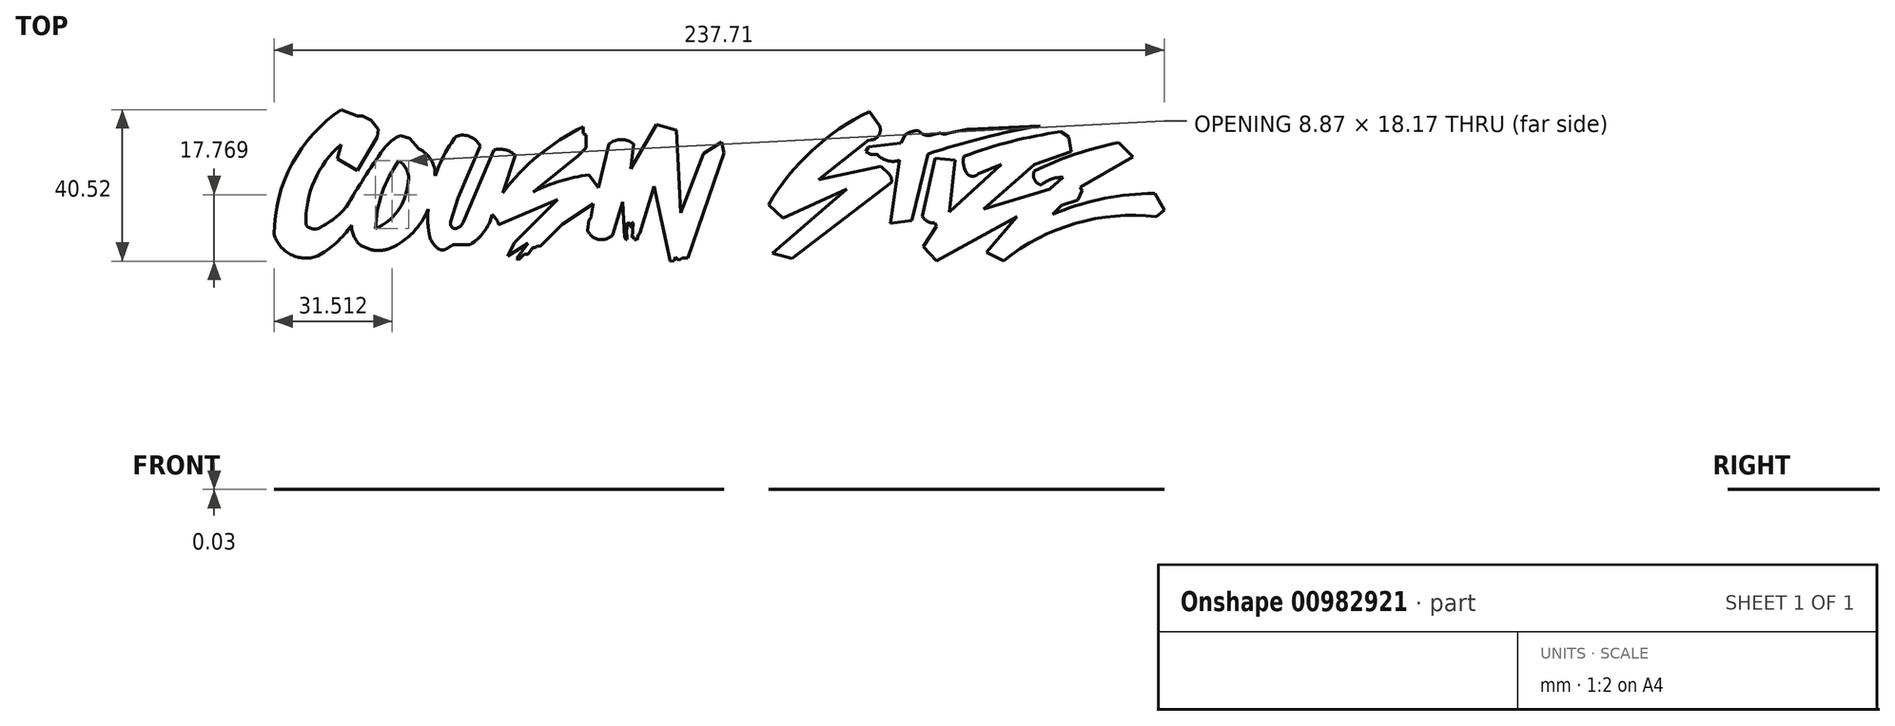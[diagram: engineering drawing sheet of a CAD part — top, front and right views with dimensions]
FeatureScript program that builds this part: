
annotation { "Feature Type Name" : "Feature", "Feature Type Description" : "" }
export const myFeature = defineFeature(function(context is Context, id is Id, definition is map)
    precondition{}
    {
        {
            var Q0;
            Q0=qCreatedBy(makeId("Top.planeOp"),FACE);
            var sketch = newSketch(context, id + "F0", { "sketchPlane" : qUnion([Q0])});
            skLineSegment(sketch, "E0", {"start": v(-35.46, -23.34) * mm, "end": v(-30.17, -14.33) * mm});
            skLineSegment(sketch, "E1", {"start": v(-30.17, -14.33) * mm, "end": v(-29.84, -12.23) * mm});
            skLineSegment(sketch, "E2", {"start": v(-29.84, -12.23) * mm, "end": v(-31.77, -9.82) * mm});
            skLineSegment(sketch, "E3", {"start": v(-31.77, -9.82) * mm, "end": v(-34.06, -8.67) * mm});
            skLineSegment(sketch, "E4", {"start": v(-34.06, -8.67) * mm, "end": v(-35.46, -8.67) * mm});
            skLineSegment(sketch, "E5", {"start": v(-35.46, -8.67) * mm, "end": v(-39.77, -7) * mm});
            skArc(sketch, "E6", {"start": v(-39.77, -7) * mm, "mid": v(-52.88, -21.43) * mm, "end": v(-57.73, -40.32) * mm});
            skArc(sketch, "E7", {"start": v(-57.73, -40.32) * mm, "mid": v(-53.23, -45.73) * mm, "end": v(-46.2, -46.17) * mm});
            skArc(sketch, "E8", {"start": v(-46.2, -46.17) * mm, "mid": v(-41.12, -42.57) * mm, "end": v(-37.05, -37.85) * mm});
            skArc(sketch, "E9", {"start": v(-37.05, -37.85) * mm, "mid": v(-36.37, -40.9) * mm, "end": v(-34.48, -43.39) * mm});
            skLineSegment(sketch, "E10", {"start": v(-34.48, -43.39) * mm, "end": v(-31.63, -44.47) * mm});
            skArc(sketch, "E11", {"start": v(-31.63, -44.47) * mm, "mid": v(-29.09, -44.6) * mm, "end": v(-26.6, -44.04) * mm});
            skArc(sketch, "E12", {"start": v(-26.6, -44.04) * mm, "mid": v(-20.56, -39.76) * mm, "end": v(-16.55, -33.54) * mm});
            skArc(sketch, "E13", {"start": v(-16.55, -33.54) * mm, "mid": v(-16.67, -36) * mm, "end": v(-16.55, -38.47) * mm});
            skArc(sketch, "E14", {"start": v(-16.55, -38.47) * mm, "mid": v(-16.38, -39.69) * mm, "end": v(-16.17, -40.9) * mm});
            skArc(sketch, "E15", {"start": v(-16.17, -40.9) * mm, "mid": v(-15.26, -42.78) * mm, "end": v(-13.74, -44.22) * mm});
            skArc(sketch, "E16", {"start": v(-13.74, -44.22) * mm, "mid": v(-12.76, -44.51) * mm, "end": v(-11.77, -44.22) * mm});
            skArc(sketch, "E17", {"start": v(-11.77, -44.22) * mm, "mid": v(-10.82, -43.68) * mm, "end": v(-9.93, -43.06) * mm});
            skLineSegment(sketch, "E18", {"start": v(-9.93, -43.06) * mm, "end": v(-5.36, -43.06) * mm});
            skArc(sketch, "E19", {"start": v(-5.36, -43.06) * mm, "mid": v(-1.64, -39.67) * mm, "end": v(0.5, -35.13) * mm});
            skArc(sketch, "E20", {"start": v(2.27, -37.75) * mm, "mid": v(1.61, -36.3) * mm, "end": v(0.5, -35.13) * mm});
            skLineSegment(sketch, "E21", {"start": v(2.27, -37.75) * mm, "end": v(17.92, -31.07) * mm});
            skLineSegment(sketch, "E22", {"start": v(17.92, -31.07) * mm, "end": v(6.59, -42.5) * mm});
            skLineSegment(sketch, "E23", {"start": v(6.59, -42.5) * mm, "end": v(4.59, -46.12) * mm});
            skLineSegment(sketch, "E24", {"start": v(4.59, -46.12) * mm, "end": v(10.13, -42.66) * mm});
            skLineSegment(sketch, "E25", {"start": v(10.13, -42.66) * mm, "end": v(7, -46.8) * mm});
            skLineSegment(sketch, "E26", {"start": v(7, -46.8) * mm, "end": v(7.56, -47.1) * mm});
            skLineSegment(sketch, "E27", {"start": v(7.56, -47.1) * mm, "end": v(9.08, -45.58) * mm});
            skLineSegment(sketch, "E28", {"start": v(9.08, -45.58) * mm, "end": v(10.12, -45.58) * mm});
            skLineSegment(sketch, "E29", {"start": v(10.12, -45.58) * mm, "end": v(11.39, -43.92) * mm});
            skLineSegment(sketch, "E30", {"start": v(11.39, -43.92) * mm, "end": v(12.1, -43.92) * mm});
            skLineSegment(sketch, "E31", {"start": v(12.1, -43.92) * mm, "end": v(12.7, -43.32) * mm});
            skLineSegment(sketch, "E32", {"start": v(12.7, -43.32) * mm, "end": v(13.26, -43.63) * mm});
            skLineSegment(sketch, "E33", {"start": v(13.26, -43.63) * mm, "end": v(19.23, -37.6) * mm});
            skLineSegment(sketch, "E34", {"start": v(19.23, -37.6) * mm, "end": v(27.54, -32.23) * mm});
            skLineSegment(sketch, "E35", {"start": v(27.54, -32.23) * mm, "end": v(26.9, -36) * mm});
            skLineSegment(sketch, "E36", {"start": v(26.9, -36) * mm, "end": v(26.4, -36.5) * mm});
            skLineSegment(sketch, "E37", {"start": v(26.4, -36.5) * mm, "end": v(26.02, -39.3) * mm});
            skArc(sketch, "E38", {"start": v(26.02, -39.3) * mm, "mid": v(29.05, -41.7) * mm, "end": v(32.72, -40.48) * mm});
            skLineSegment(sketch, "E39", {"start": v(32.72, -40.48) * mm, "end": v(35.35, -31.71) * mm});
            skLineSegment(sketch, "E40", {"start": v(35.35, -31.71) * mm, "end": v(35.84, -41.17) * mm});
            skLineSegment(sketch, "E41", {"start": v(35.84, -41.17) * mm, "end": v(36.3, -41.72) * mm});
            skLineSegment(sketch, "E42", {"start": v(36.3, -41.72) * mm, "end": v(36.58, -41.72) * mm});
            skLineSegment(sketch, "E43", {"start": v(36.58, -41.72) * mm, "end": v(36.4, -38.94) * mm});
            skLineSegment(sketch, "E44", {"start": v(36.4, -38.94) * mm, "end": v(36.56, -38.93) * mm});
            skLineSegment(sketch, "E45", {"start": v(36.56, -38.93) * mm, "end": v(36.56, -37.23) * mm});
            skLineSegment(sketch, "E46", {"start": v(36.56, -37.23) * mm, "end": v(37.18, -37.42) * mm});
            skLineSegment(sketch, "E47", {"start": v(37.18, -37.42) * mm, "end": v(37.23, -38.22) * mm});
            skLineSegment(sketch, "E48", {"start": v(37.23, -38.22) * mm, "end": v(37.51, -38.3) * mm});
            skLineSegment(sketch, "E49", {"start": v(37.51, -38.3) * mm, "end": v(37.85, -37.2) * mm});
            skLineSegment(sketch, "E50", {"start": v(37.85, -37.2) * mm, "end": v(38.18, -37.3) * mm});
            skLineSegment(sketch, "E51", {"start": v(38.18, -37.3) * mm, "end": v(37.92, -41.18) * mm});
            skLineSegment(sketch, "E52", {"start": v(37.92, -41.18) * mm, "end": v(38.56, -41.23) * mm});
            skLineSegment(sketch, "E53", {"start": v(38.56, -41.23) * mm, "end": v(38.58, -41.65) * mm});
            skLineSegment(sketch, "E54", {"start": v(38.58, -41.65) * mm, "end": v(39.19, -41.84) * mm});
            skLineSegment(sketch, "E55", {"start": v(39.19, -41.84) * mm, "end": v(39.62, -40.4) * mm});
            skLineSegment(sketch, "E56", {"start": v(39.62, -40.4) * mm, "end": v(40, -40.04) * mm});
            skLineSegment(sketch, "E57", {"start": v(40, -40.04) * mm, "end": v(43.78, -27.45) * mm});
            skLineSegment(sketch, "E58", {"start": v(43.78, -27.45) * mm, "end": v(47.87, -46.66) * mm});
            skLineSegment(sketch, "E59", {"start": v(47.87, -46.66) * mm, "end": v(48.05, -47.51) * mm});
            skLineSegment(sketch, "E60", {"start": v(48.05, -47.51) * mm, "end": v(49.14, -47.46) * mm});
            skLineSegment(sketch, "E61", {"start": v(49.14, -47.46) * mm, "end": v(49.45, -46.45) * mm});
            skLineSegment(sketch, "E62", {"start": v(49.45, -46.45) * mm, "end": v(50.43, -47.31) * mm});
            skLineSegment(sketch, "E63", {"start": v(50.43, -47.31) * mm, "end": v(51.29, -46.67) * mm});
            skLineSegment(sketch, "E64", {"start": v(51.29, -46.67) * mm, "end": v(52.83, -46.6) * mm});
            skLineSegment(sketch, "E65", {"start": v(52.83, -46.6) * mm, "end": v(62.42, -18.6) * mm});
            skLineSegment(sketch, "E66", {"start": v(62.42, -18.6) * mm, "end": v(61.79, -15.64) * mm});
            skLineSegment(sketch, "E67", {"start": v(61.79, -15.64) * mm, "end": v(57.03, -18.7) * mm});
            skLineSegment(sketch, "E68", {"start": v(57.03, -18.7) * mm, "end": v(50.9, -34.63) * mm});
            skLineSegment(sketch, "E69", {"start": v(50.9, -34.63) * mm, "end": v(49.75, -12.54) * mm});
            skLineSegment(sketch, "E70", {"start": v(49.75, -12.54) * mm, "end": v(44.44, -10.95) * mm});
            skLineSegment(sketch, "E71", {"start": v(37.51, -22.74) * mm, "end": v(38.31, -16.14) * mm});
            skArc(sketch, "E72", {"start": v(38.31, -16.14) * mm, "mid": v(35.02, -15.01) * mm, "end": v(31.74, -16.14) * mm});
            skLineSegment(sketch, "E73", {"start": v(31.74, -16.14) * mm, "end": v(28.92, -27.87) * mm});
            skLineSegment(sketch, "E74", {"start": v(44.44, -10.95) * mm, "end": v(37.51, -22.74) * mm});
            skLineSegment(sketch, "E75", {"start": v(28.92, -27.87) * mm, "end": v(26.31, -24.41) * mm});
            skArc(sketch, "E76", {"start": v(26.31, -24.41) * mm, "mid": v(18.73, -26.07) * mm, "end": v(11.53, -28.94) * mm});
            skLineSegment(sketch, "E77", {"start": v(11.53, -28.94) * mm, "end": v(23.38, -19.3) * mm});
            skLineSegment(sketch, "E78", {"start": v(23.38, -19.3) * mm, "end": v(25.6, -17.2) * mm});
            skLineSegment(sketch, "E79", {"start": v(25.6, -17.2) * mm, "end": v(25.6, -13.81) * mm});
            skLineSegment(sketch, "E80", {"start": v(25.6, -13.81) * mm, "end": v(24.79, -13.37) * mm});
            skLineSegment(sketch, "E81", {"start": v(24.79, -13.37) * mm, "end": v(24.79, -11.64) * mm});
            skArc(sketch, "E82", {"start": v(24.79, -11.64) * mm, "mid": v(13, -19.15) * mm, "end": v(3.32, -29.24) * mm});
            skLineSegment(sketch, "E83", {"start": v(3.32, -29.24) * mm, "end": v(6.7, -19.23) * mm});
            skArc(sketch, "E84", {"start": v(6.7, -19.23) * mm, "mid": v(4.06, -17.73) * mm, "end": v(1.03, -17.78) * mm});
            skLineSegment(sketch, "E85", {"start": v(1.03, -17.78) * mm, "end": v(-7.16, -37.03) * mm});
            skArc(sketch, "E86", {"start": v(-9.42, -38.84) * mm, "mid": v(-8.06, -38.22) * mm, "end": v(-7.16, -37.03) * mm});
            skArc(sketch, "E87", {"start": v(-10.54, -37.03) * mm, "mid": v(-10.4, -38.19) * mm, "end": v(-9.42, -38.84) * mm});
            skLineSegment(sketch, "E88", {"start": v(-10.54, -37.03) * mm, "end": v(-8.5, -30.48) * mm});
            skLineSegment(sketch, "E89", {"start": v(-8.5, -30.48) * mm, "end": v(-2.67, -16.75) * mm});
            skArc(sketch, "E90", {"start": v(-2.67, -16.75) * mm, "mid": v(-5.37, -14.22) * mm, "end": v(-9.07, -14.1) * mm});
            skArc(sketch, "E91", {"start": v(-9.07, -14.1) * mm, "mid": v(-12.31, -19.16) * mm, "end": v(-14.72, -24.67) * mm});
            skArc(sketch, "E92", {"start": v(-14.72, -24.67) * mm, "mid": v(-15.84, -20.37) * mm, "end": v(-19.13, -17.4) * mm});
            skLineSegment(sketch, "E93", {"start": v(-19.13, -17.4) * mm, "end": v(-21.48, -14.69) * mm});
            skLineSegment(sketch, "E94", {"start": v(-21.48, -14.69) * mm, "end": v(-24.11, -13.93) * mm});
            skArc(sketch, "E95", {"start": v(-24.11, -13.93) * mm, "mid": v(-26.6, -15.53) * mm, "end": v(-28.58, -17.7) * mm});
            skArc(sketch, "E96", {"start": v(-28.58, -17.7) * mm, "mid": v(-33.65, -25.22) * mm, "end": v(-38.4, -32.94) * mm});
            skArc(sketch, "E97", {"start": v(-44.8, -38.08) * mm, "mid": v(-41.31, -35.86) * mm, "end": v(-38.4, -32.94) * mm});
            skArc(sketch, "E98", {"start": v(-49.21, -37.8) * mm, "mid": v(-47.07, -38.9) * mm, "end": v(-44.8, -38.08) * mm});
            skArc(sketch, "E99", {"start": v(-39.78, -16.26) * mm, "mid": v(-46.96, -25.95) * mm, "end": v(-49.21, -37.8) * mm});
            skLineSegment(sketch, "E100", {"start": v(-39.78, -16.26) * mm, "end": v(-40.81, -20.06) * mm});
            skLineSegment(sketch, "E101", {"start": v(-40.81, -20.06) * mm, "end": v(-35.46, -23.34) * mm});
            skArc(sketch, "E102", {"start": v(-22.07, -27.05) * mm, "mid": v(-22.12, -23.44) * mm, "end": v(-24.4, -20.66) * mm});
            skArc(sketch, "E103", {"start": v(-30.65, -38.83) * mm, "mid": v(-24.7, -34.14) * mm, "end": v(-22.07, -27.05) * mm});
            skArc(sketch, "E104", {"start": v(-24.4, -20.66) * mm, "mid": v(-28.86, -29.28) * mm, "end": v(-30.65, -38.83) * mm});
            skLineSegment(sketch, "E105", {"start": v(80.59, -46.78) * mm, "end": v(107.16, -26.42) * mm});
            skArc(sketch, "E106", {"start": v(107.16, -26.42) * mm, "mid": v(107.1, -25.22) * mm, "end": v(106.47, -24.2) * mm});
            skLineSegment(sketch, "E107", {"start": v(106.47, -24.2) * mm, "end": v(104.3, -22.12) * mm});
            skLineSegment(sketch, "E108", {"start": v(104.3, -22.12) * mm, "end": v(87.65, -25.65) * mm});
            skLineSegment(sketch, "E109", {"start": v(87.65, -25.65) * mm, "end": v(101.15, -15.1) * mm});
            skArc(sketch, "E110", {"start": v(101.15, -15.1) * mm, "mid": v(103.72, -13.93) * mm, "end": v(103.9, -11.11) * mm});
            skLineSegment(sketch, "E111", {"start": v(103.9, -11.11) * mm, "end": v(101.26, -7.48) * mm});
            skArc(sketch, "E112", {"start": v(101.26, -7.48) * mm, "mid": v(85.96, -17.95) * mm, "end": v(74.33, -32.39) * mm});
            skLineSegment(sketch, "E113", {"start": v(74.33, -32.39) * mm, "end": v(78.12, -36) * mm});
            skLineSegment(sketch, "E114", {"start": v(78.12, -36) * mm, "end": v(95.15, -28.29) * mm});
            skLineSegment(sketch, "E115", {"start": v(95.15, -28.29) * mm, "end": v(75.38, -45.37) * mm});
            skLineSegment(sketch, "E116", {"start": v(75.38, -45.37) * mm, "end": v(80.59, -46.78) * mm});
            skArc(sketch, "E117", {"start": v(103.41, -19.02) * mm, "mid": v(106.16, -20.65) * mm, "end": v(109.34, -20.52) * mm});
            skLineSegment(sketch, "E118", {"start": v(103.41, -19.02) * mm, "end": v(101.64, -19.02) * mm});
            skLineSegment(sketch, "E119", {"start": v(101.64, -19.02) * mm, "end": v(100.28, -18.2) * mm});
            skLineSegment(sketch, "E120", {"start": v(100.28, -18.2) * mm, "end": v(101.04, -16.93) * mm});
            skLineSegment(sketch, "E121", {"start": v(101.04, -16.93) * mm, "end": v(109.68, -15.95) * mm});
            skLineSegment(sketch, "E122", {"start": v(109.68, -15.95) * mm, "end": v(110.78, -13.7) * mm});
            skArc(sketch, "E123", {"start": v(114.41, -12.56) * mm, "mid": v(112.52, -12.9) * mm, "end": v(110.78, -13.7) * mm});
            skArc(sketch, "E124", {"start": v(114.41, -12.56) * mm, "mid": v(116, -13.76) * mm, "end": v(117.98, -13.7) * mm});
            skLineSegment(sketch, "E125", {"start": v(117.98, -13.7) * mm, "end": v(120.12, -13.2) * mm});
            skArc(sketch, "E126", {"start": v(120.12, -13.2) * mm, "mid": v(121.24, -13.5) * mm, "end": v(122.36, -13.2) * mm});
            skLineSegment(sketch, "E127", {"start": v(122.36, -13.2) * mm, "end": v(127.47, -12.3) * mm});
            skLineSegment(sketch, "E128", {"start": v(127.47, -12.3) * mm, "end": v(146.86, -11.3) * mm});
            skArc(sketch, "E129", {"start": v(146.86, -11.3) * mm, "mid": v(131.75, -14.52) * mm, "end": v(116.9, -18.84) * mm});
            skLineSegment(sketch, "E130", {"start": v(116.9, -18.84) * mm, "end": v(112.61, -36.62) * mm});
            skLineSegment(sketch, "E131", {"start": v(112.61, -36.62) * mm, "end": v(106.85, -37.36) * mm});
            skLineSegment(sketch, "E132", {"start": v(106.85, -37.36) * mm, "end": v(109.34, -20.52) * mm});
            skLineSegment(sketch, "E133", {"start": v(118.82, -19.94) * mm, "end": v(124.09, -20.52) * mm});
            skLineSegment(sketch, "E134", {"start": v(124.09, -20.52) * mm, "end": v(122.56, -34.35) * mm});
            skLineSegment(sketch, "E135", {"start": v(122.56, -34.35) * mm, "end": v(136.42, -21.67) * mm});
            skLineSegment(sketch, "E136", {"start": v(136.42, -21.67) * mm, "end": v(130.26, -24.2) * mm});
            skArc(sketch, "E137", {"start": v(127.44, -24.2) * mm, "mid": v(128.85, -24.81) * mm, "end": v(130.26, -24.2) * mm});
            skArc(sketch, "E138", {"start": v(126.44, -19.53) * mm, "mid": v(126.46, -21.96) * mm, "end": v(127.44, -24.2) * mm});
            skArc(sketch, "E139", {"start": v(152.29, -12.92) * mm, "mid": v(139.17, -15.48) * mm, "end": v(126.44, -19.53) * mm});
            skLineSegment(sketch, "E140", {"start": v(152.29, -12.92) * mm, "end": v(154.49, -14.29) * mm});
            skLineSegment(sketch, "E141", {"start": v(154.49, -14.29) * mm, "end": v(155.2, -18.2) * mm});
            skLineSegment(sketch, "E142", {"start": v(155.2, -18.2) * mm, "end": v(145.3, -21.64) * mm});
            skLineSegment(sketch, "E143", {"start": v(145.3, -21.64) * mm, "end": v(131.75, -33.54) * mm});
            skPoint(sketch, "E143.endSnap0", {"position": v(131.75, -14.52) * mm});
            skLineSegment(sketch, "E144", {"start": v(131.75, -33.54) * mm, "end": v(149.47, -28.18) * mm});
            skLineSegment(sketch, "E145", {"start": v(149.47, -28.18) * mm, "end": v(152.93, -25.1) * mm});
            skArc(sketch, "E146", {"start": v(152.93, -25.1) * mm, "mid": v(149.86, -25.56) * mm, "end": v(147.18, -27.13) * mm});
            skArc(sketch, "E147", {"start": v(145.28, -23.47) * mm, "mid": v(145.38, -25.74) * mm, "end": v(147.18, -27.13) * mm});
            skArc(sketch, "E148", {"start": v(167.87, -15.76) * mm, "mid": v(156.33, -18.88) * mm, "end": v(145.28, -23.47) * mm});
            skLineSegment(sketch, "E149", {"start": v(167.87, -15.76) * mm, "end": v(171.62, -19.6) * mm});
            skLineSegment(sketch, "E150", {"start": v(171.62, -19.6) * mm, "end": v(157.5, -27.7) * mm});
            skLineSegment(sketch, "E151", {"start": v(157.5, -27.7) * mm, "end": v(158.04, -28.64) * mm});
            skLineSegment(sketch, "E152", {"start": v(158.04, -28.64) * mm, "end": v(156.92, -31.21) * mm});
            skLineSegment(sketch, "E153", {"start": v(156.92, -31.21) * mm, "end": v(152.6, -32.58) * mm});
            skLineSegment(sketch, "E154", {"start": v(152.6, -32.58) * mm, "end": v(150.18, -35.02) * mm});
            skArc(sketch, "E155", {"start": v(175.54, -29.41) * mm, "mid": v(162.6, -31.03) * mm, "end": v(150.18, -35.02) * mm});
            skLineSegment(sketch, "E156", {"start": v(175.54, -29.41) * mm, "end": v(177.53, -29.35) * mm});
            skLineSegment(sketch, "E157", {"start": v(177.53, -29.35) * mm, "end": v(179.98, -33.8) * mm});
            skLineSegment(sketch, "E158", {"start": v(179.98, -33.8) * mm, "end": v(177.87, -35.63) * mm});
            skArc(sketch, "E159", {"start": v(177.87, -35.63) * mm, "mid": v(156.28, -37.4) * mm, "end": v(137.06, -47.4) * mm});
            skLineSegment(sketch, "E160", {"start": v(137.06, -47.4) * mm, "end": v(132.48, -45.1) * mm});
            skLineSegment(sketch, "E161", {"start": v(132.48, -45.1) * mm, "end": v(140.67, -35.62) * mm});
            skLineSegment(sketch, "E162", {"start": v(140.67, -35.62) * mm, "end": v(119.25, -47.4) * mm});
            skLineSegment(sketch, "E163", {"start": v(119.25, -47.4) * mm, "end": v(115.66, -43.67) * mm});
            skLineSegment(sketch, "E164", {"start": v(115.66, -43.67) * mm, "end": v(119.25, -38.2) * mm});
            skLineSegment(sketch, "E165", {"start": v(119.25, -38.2) * mm, "end": v(118.74, -37.28) * mm});
            skArc(sketch, "E166", {"start": v(115.38, -35.45) * mm, "mid": v(116.78, -36.88) * mm, "end": v(118.74, -37.28) * mm});
            skLineSegment(sketch, "E167", {"start": v(115.38, -35.45) * mm, "end": v(118.82, -19.94) * mm});
            skSolve(sketch);
        }
        {
            var Q0;
            Q0 = qSketchRegion(id + "F0", true);
            extrude(context, id + "F1", {"entities" : qUnion([Q0]), "depth" : 0.03 * mm, "offsetDistance" : 25.4 * mm});
        }
    });
